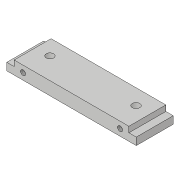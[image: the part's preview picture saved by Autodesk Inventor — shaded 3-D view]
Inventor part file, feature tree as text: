
AUTODESK INVENTOR PART (.ipt)
format: ipt  version: 2018.3 (Build 223284000, 284)  size: 150,016 bytes
history: native  units: in
note: dims shown in document units (in); Inventor stores cm internally (conversion verified against a paired STEP export)
features: extrude x3, sketch x3, hole x2
ambient origin geometry x8: Origin, YZ Plane, XZ Plane, XY Plane, X Axis, Y Axis, Z Axis, Center Point
bodies: Solid1 (feature_tree)
feature tree (8):
  extrude  "Extrusion1"  Depth=0.625in
  extrude  "Extrusion6"  Depth=0.221in
  extrude  "Extrusion7"  Depth=0.125in
  hole  "Hole3"  [1 undecoded]
  hole  "Hole4"  [1 undecoded]
  sketch  "Sketch1"  dims[d0=2.1903in d1=0.625in]
  sketch  "Sketch7"  dims[d2=0.221in d3=0.0in d22=0.126in]
  sketch  "Sketch8"  dims[d23=0.126in d24=1.4567in d32=1.0in d33=0.0in d34=0.125in d35=0.125in d36=0.096in d37=0.0in d43=0.2619in d44=0.2619in d48=0.367in d49=0.3666in d69=0.15in d70=0.1105in d71=0.085in d72=0.224in d73=0.375in d74=0.25in d75=0.5635in d76=0.125in d77=0.8108in d78=0.15in d79=0.1105in d80=0.085in d81=0.224in d82=0.375in d83=0.25in d84=0.5635in d85=0.125in d86=0.8108in]
note: 2 required parameter values undecoded (feature->parameter linkage not recoverable at this tier; creation-order binding heuristic only, values carry confidence <= 0.55)
